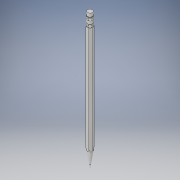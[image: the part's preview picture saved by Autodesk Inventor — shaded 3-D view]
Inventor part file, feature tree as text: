
AUTODESK INVENTOR PART (.ipt)
format: ipt  version: 2017 (Build 210142000, 142)  size: 200,192 bytes
history: native  units: in
note: dims shown in document units (in); Inventor stores cm internally (conversion verified against a paired STEP export)
features: other x5, sketch x5, extrude x2
ambient origin geometry x8: Origin, YZ Plane, XZ Plane, XY Plane, X Axis, Y Axis, Z Axis, Center Point
bodies: Body1 (feature_tree), Body2 (feature_tree)
feature tree (12):
  other  "pencil"
  extrude  "wooden part of pencil"  Depth=0.5578in TaperAngle=0.0deg
  extrude  "pencil graphite"  Depth=0.0047in
  other  "connection for pencil and eraser"
  other  "eraser"
  other  "sharpen pencil"
  sketch  "Sketch1"  dims[d0=0.023in d1=0.5578in d2=0.0in]
  sketch  "Sketch3"  dims[d3=0.0122in d4=0.0047in]
  sketch  "Sketch4"  dims[d10=0.0019in]
  sketch  "Sketch5"  dims[d13=0.0027in]
  other  "graphite"
  sketch  "Sketch6"  dims[d14=0.0167in d15=0.0045in d16=0.0019in d17=0.0028in d18=0.0014in d20=0.0013in d21=0.0005in d22=0.0027in d23=0.0027in d24=0.0027in d25=0.0027in d26=0.0027in d27=0.0019in d28=0.0018in d29=0.0019in d30=90.0deg d31=0.011in d32=0.0154in d33=90.0deg d34=0.006in d35=0.006in d36=1.0in d37=0.0in d39=0.1237in d41=90.0deg]
